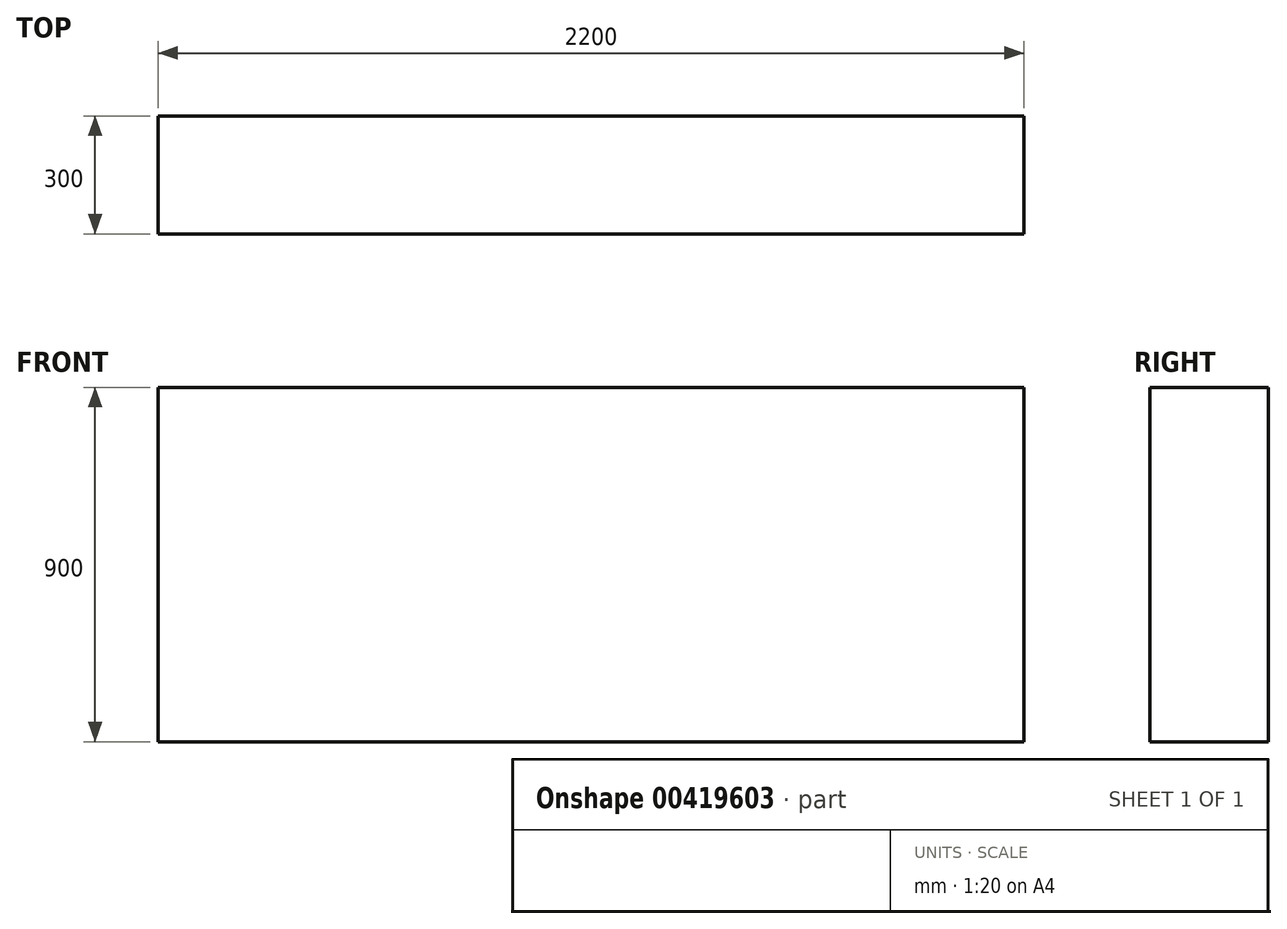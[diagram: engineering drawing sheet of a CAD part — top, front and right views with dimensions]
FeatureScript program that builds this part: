
annotation { "Feature Type Name" : "Feature", "Feature Type Description" : "" }
export const myFeature = defineFeature(function(context is Context, id is Id, definition is map)
    precondition{}
    {
        {
            var Q0;
            Q0=qCreatedBy(makeId("Top.planeOp"),FACE);
            var sketch = newSketch(context, id + "F0", { "sketchPlane" : qUnion([Q0])});
            skLineSegment(sketch, "E0.bottom", {"start": v(-2081.05, 247) * mm, "end": v(118.95, 247) * mm});
            skLineSegment(sketch, "E0.top", {"start": v(-2081.05, -53) * mm, "end": v(118.95, -53) * mm});
            skLineSegment(sketch, "E0.left", {"start": v(-2081.05, 247) * mm, "end": v(-2081.05, -53) * mm});
            skLineSegment(sketch, "E0.right", {"start": v(118.95, 247) * mm, "end": v(118.95, -53) * mm});
            skSolve(sketch);
        }
        {
            var Q0;
            Q0=makeQuery(id+"F0.imprint","IMPRINT",FACE,{"disambiguationData":[TD([[makeQuery(id+"F0.imprint","IMPRINT",EDGE,{"derivedFrom":sQuery(id+"F0.wireOp",EDGE,"E0.bottom")}),-1.0]])]});
            extrude(context, id + "F1", {"entities" : qUnion([Q0]), "depth" : 900 * mm});
        }
    });
